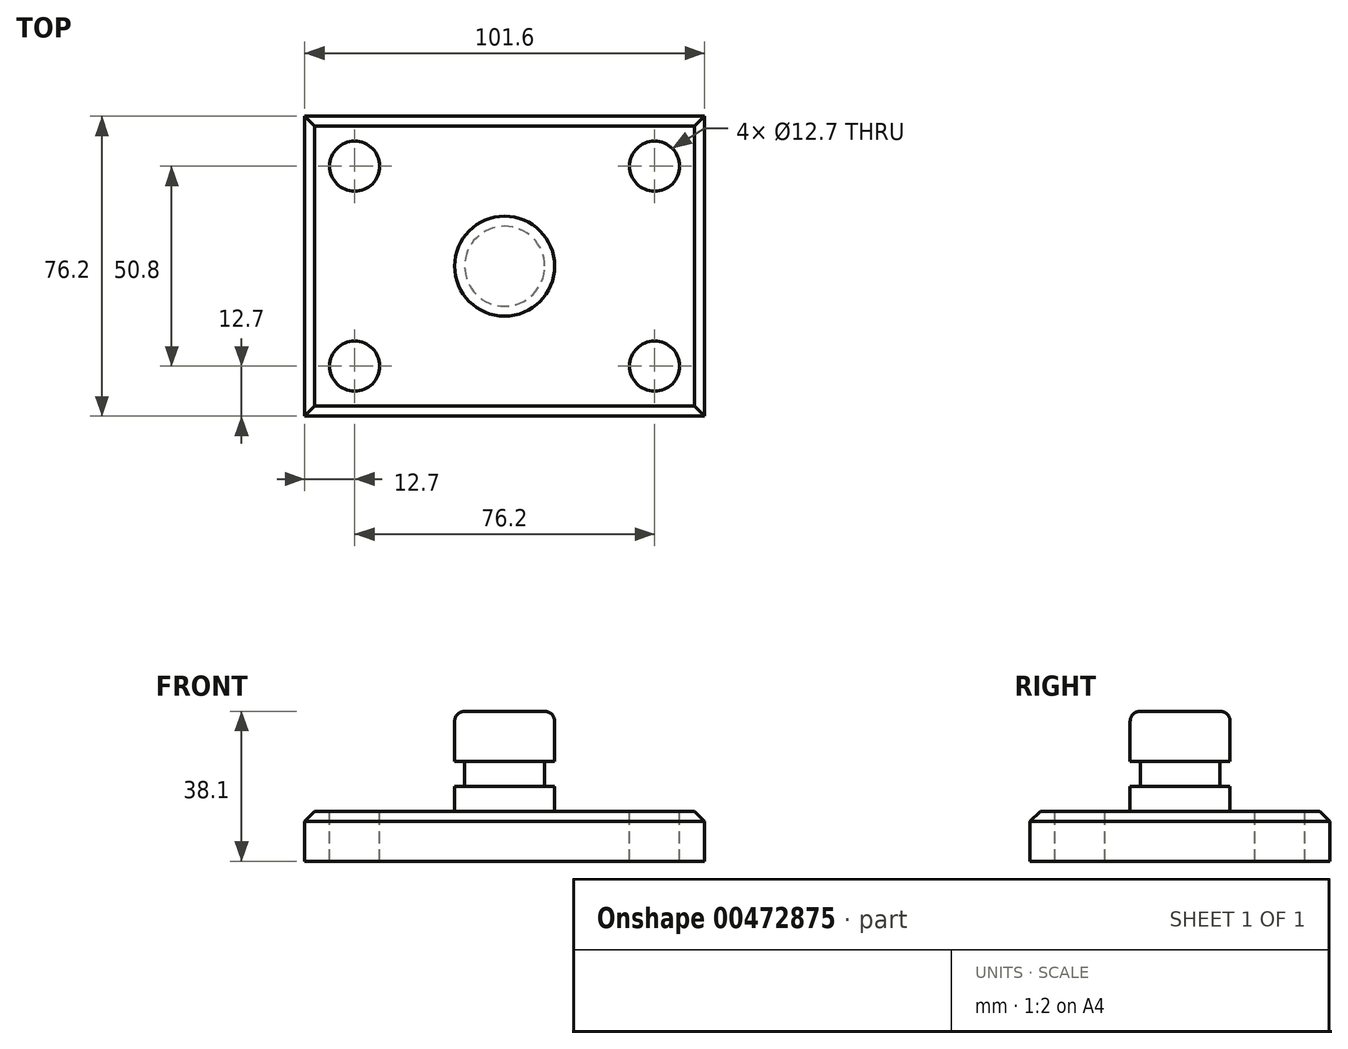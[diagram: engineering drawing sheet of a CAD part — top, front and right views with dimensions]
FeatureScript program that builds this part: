
annotation { "Feature Type Name" : "Feature", "Feature Type Description" : "" }
export const myFeature = defineFeature(function(context is Context, id is Id, definition is map)
    precondition{}
    {
        {
            var Q0;
            Q0=qCreatedBy(makeId("Top.planeOp"),FACE);
            var sketch = newSketch(context, id + "F0", { "sketchPlane" : qUnion([Q0])});
            skLineSegment(sketch, "E0.bottom", {"start": v(50.8, -38.1) * mm, "end": v(-50.8, -38.1) * mm});
            skLineSegment(sketch, "E0.top", {"start": v(50.8, 38.1) * mm, "end": v(-50.8, 38.1) * mm});
            skLineSegment(sketch, "E0.left", {"start": v(50.8, -38.1) * mm, "end": v(50.8, 38.1) * mm});
            skLineSegment(sketch, "E0.right", {"start": v(-50.8, -38.1) * mm, "end": v(-50.8, 38.1) * mm});
            skPoint(sketch, "E0.middle", {"position": v(0, 0) * mm});
            skSolve(sketch);
        }
        {
            var Q0;
            Q0=makeQuery(id+"F0.imprint","IMPRINT",FACE,{"disambiguationData":[TD([[makeQuery(id+"F0.imprint","IMPRINT",EDGE,{"derivedFrom":sQuery(id+"F0.wireOp",EDGE,"E0.bottom")}),-1.0]])]});
            extrude(context, id + "F1", {"entities" : qUnion([Q0]), "depth" : 12.7 * mm});
        }
        {
            var Q0;
            Q0=makeQuery(id+"F1.opExtrude","CAP_FACE",FACE,{"disambiguationData":[OSD([sQuery(id+"F0.wireOp",EDGE,"E0.bottom"),sQuery(id+"F0.wireOp",EDGE,"E0.top"),sQuery(id+"F0.wireOp",EDGE,"E0.left"),sQuery(id+"F0.wireOp",EDGE,"E0.right")])],"isStart":false});
            var sketch = newSketch(context, id + "F2", { "sketchPlane" : qUnion([Q0])});
            skCircle(sketch, "E1", {"center": v(-38.1, 25.4) * mm, "radius": 6.35 * mm});
            skCircle(sketch, "E2", {"center": v(-38.1, -25.4) * mm, "radius": 6.35 * mm});
            skCircle(sketch, "E3", {"center": v(38.1, 25.4) * mm, "radius": 6.35 * mm});
            skCircle(sketch, "E4", {"center": v(38.1, -25.4) * mm, "radius": 6.35 * mm});
            skSolve(sketch);
        }
        {
            var Q0;
            Q0=makeQuery(id+"F2.imprint","IMPRINT",FACE,{"disambiguationData":[TD([[makeQuery(id+"F2.imprint","IMPRINT",EDGE,{"derivedFrom":sQuery(id+"F2.wireOp",EDGE,"E1")}),1.0]])]});
            var Q1;
            Q1=makeQuery(id+"F2.imprint","IMPRINT",FACE,{"disambiguationData":[TD([[makeQuery(id+"F2.imprint","IMPRINT",EDGE,{"derivedFrom":sQuery(id+"F2.wireOp",EDGE,"E2")}),1.0]])]});
            var Q2;
            Q2=makeQuery(id+"F2.imprint","IMPRINT",FACE,{"disambiguationData":[TD([[makeQuery(id+"F2.imprint","IMPRINT",EDGE,{"derivedFrom":sQuery(id+"F2.wireOp",EDGE,"E3")}),1.0]])]});
            var Q3;
            Q3=makeQuery(id+"F2.imprint","IMPRINT",FACE,{"disambiguationData":[TD([[makeQuery(id+"F2.imprint","IMPRINT",EDGE,{"derivedFrom":sQuery(id+"F2.wireOp",EDGE,"E4")}),1.0]])]});
            extrude(context, id + "F3", {"entities" : qUnion([Q0, Q1, Q2, Q3]), "operationType" : NewBodyOperationType.REMOVE, "endBound" : BoundingType.THROUGH_ALL, "oppositeDirection" : true, "depth" : 25.4 * mm});
        }
        {
            var Q0;
            Q0=qCreatedBy(makeId("Front.planeOp"),FACE);
            var sketch = newSketch(context, id + "F4", { "sketchPlane" : qUnion([Q0])});
            skLineSegment(sketch, "E5.bottom", {"start": v(0, 12.7) * mm, "end": v(12.7, 12.7) * mm});
            skLineSegment(sketch, "E5.top", {"start": v(0, 38.1) * mm, "end": v(12.7, 38.1) * mm});
            skLineSegment(sketch, "E5.left", {"start": v(0, 12.7) * mm, "end": v(0, 38.1) * mm});
            skLineSegment(sketch, "E5.right", {"start": v(12.7, 12.7) * mm, "end": v(12.7, 38.1) * mm});
            skSolve(sketch);
        }
        {
            var Q0;
            Q0=makeQuery(id+"F4.imprint","IMPRINT",FACE,{"disambiguationData":[TD([[makeQuery(id+"F4.imprint","IMPRINT",EDGE,{"derivedFrom":sQuery(id+"F4.wireOp",EDGE,"E5.bottom")}),1.0]])]});
            var Q1;
            Q1=sQuery(id+"F4.wireOp",EDGE,"E5.left");
            revolve(context, id + "F5", {"operationType" : NewBodyOperationType.ADD, "entities" : qUnion([Q0]), "axis" : qUnion([Q1]), "revolveType" : RevolveType.FULL});
        }
        {
            var Q0;
            Q0=qCreatedBy(makeId("Front.planeOp"),FACE);
            var sketch = newSketch(context, id + "F6", { "sketchPlane" : qUnion([Q0])});
            skLineSegment(sketch, "E6.bottom", {"start": v(14.2, 25.4) * mm, "end": v(10.16, 25.4) * mm});
            skLineSegment(sketch, "E6.top", {"start": v(14.2, 19.05) * mm, "end": v(10.16, 19.05) * mm});
            skLineSegment(sketch, "E6.left", {"start": v(14.2, 25.4) * mm, "end": v(14.2, 19.05) * mm});
            skLineSegment(sketch, "E6.right", {"start": v(10.16, 25.4) * mm, "end": v(10.16, 19.05) * mm});
            skSolve(sketch);
        }
        {
            var Q0;
            Q0=makeQuery(id+"F6.imprint","IMPRINT",FACE,{"disambiguationData":[TD([[makeQuery(id+"F6.imprint","IMPRINT",EDGE,{"derivedFrom":sQuery(id+"F6.wireOp",EDGE,"E6.bottom")}),1.0]])]});
            var Q1;
            Q1=makeQuery(id+"F5.opRevolve","SWEPT_FACE",FACE,{"disambiguationData":[OSD([sQuery(id+"F4.wireOp",EDGE,"E5.right")])]});
            revolve(context, id + "F7", {"operationType" : NewBodyOperationType.REMOVE, "entities" : qUnion([Q0]), "axis" : qUnion([Q1]), "revolveType" : RevolveType.FULL, "oppositeDirection" : true});
        }
        {
            var Q0;
            Q0=makeQuery(id+"F5.opRevolve","SWEPT_EDGE",EDGE,{"disambiguationData":[OSD([sQuery(id+"F4.wireOp",EDGE,"E5.bottom"),sQuery(id+"F4.wireOp",EDGE,"E5.right")])]});
            var Q1;
            Q1=makeQuery(id+"F5.opRevolve","SWEPT_EDGE",EDGE,{"disambiguationData":[OSD([sQuery(id+"F4.wireOp",EDGE,"E5.top"),sQuery(id+"F4.wireOp",EDGE,"E5.right")])]});
            fillet(context, id + "F8", {"entities" : qUnion([Q0, Q1]), "radius" : 2.54 * mm, "tangentPropagation" : true, "allowEdgeOverflow" : false});
        }
        {
            var Q0;
            Q0=makeQuery(id+"F1.opExtrude","CAP_EDGE",EDGE,{"disambiguationData":[OSD([sQuery(id+"F0.wireOp",EDGE,"E0.bottom")])],"isStart":false});
            var Q1;
            Q1=makeQuery(id+"F1.opExtrude","CAP_EDGE",EDGE,{"disambiguationData":[OSD([sQuery(id+"F0.wireOp",EDGE,"E0.left")])],"isStart":false});
            var Q2;
            Q2=makeQuery(id+"F1.opExtrude","CAP_EDGE",EDGE,{"disambiguationData":[OSD([sQuery(id+"F0.wireOp",EDGE,"E0.top")])],"isStart":false});
            var Q3;
            Q3=makeQuery(id+"F1.opExtrude","CAP_EDGE",EDGE,{"disambiguationData":[OSD([sQuery(id+"F0.wireOp",EDGE,"E0.right")])],"isStart":false});
            chamfer(context, id + "F9", {"entities" : qUnion([Q0, Q1, Q2, Q3]), "width" : 2.54 * mm, "tangentPropagation" : true});
        }
    });
